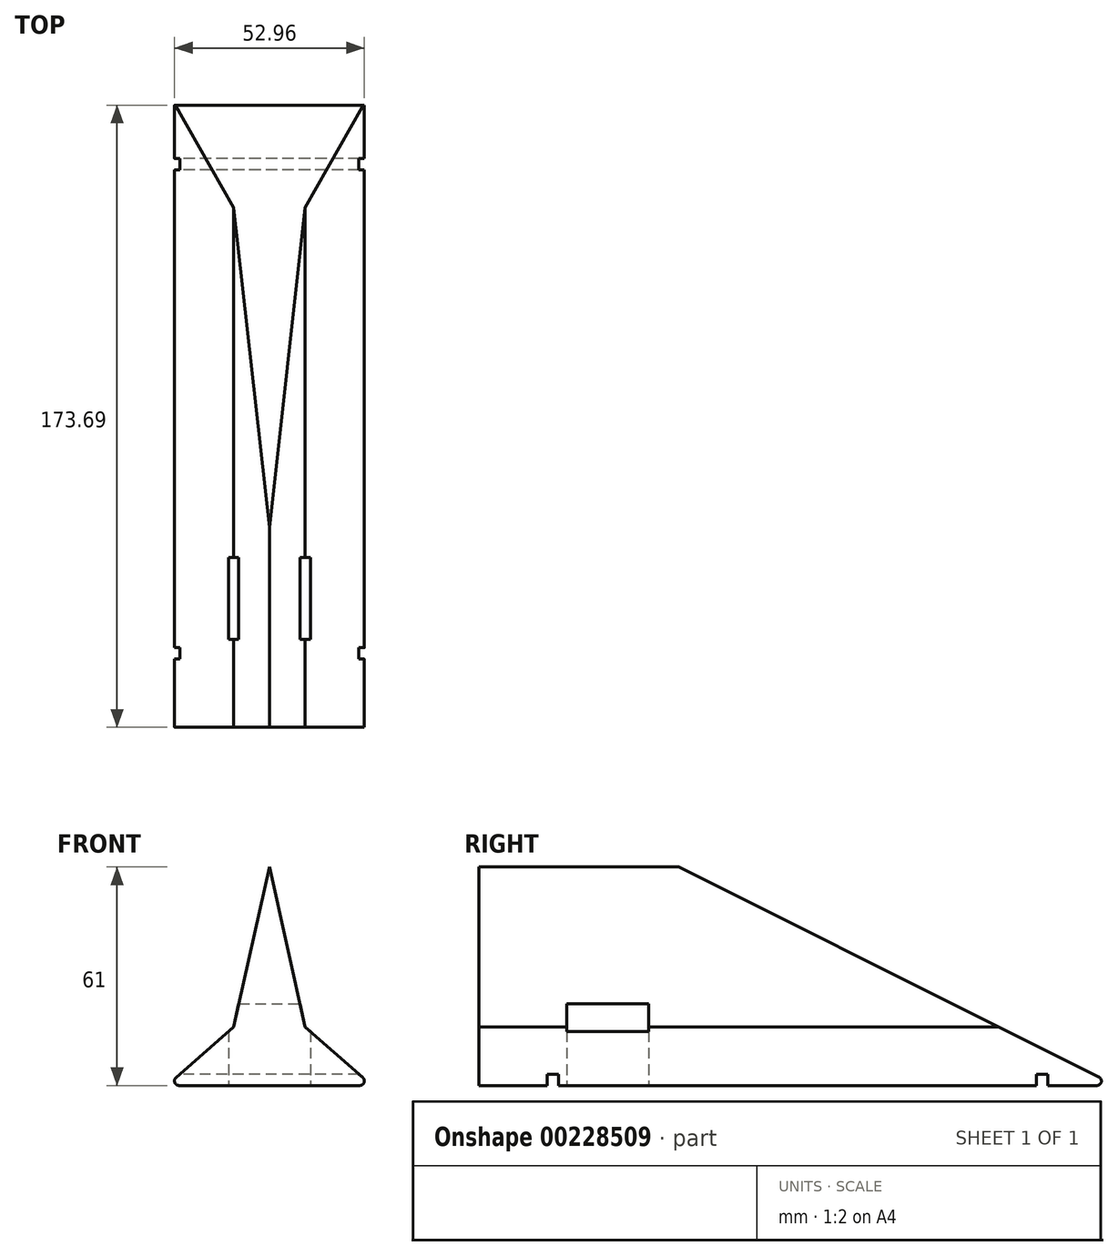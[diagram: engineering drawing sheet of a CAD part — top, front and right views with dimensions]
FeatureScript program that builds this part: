
annotation { "Feature Type Name" : "Feature", "Feature Type Description" : "" }
export const myFeature = defineFeature(function(context is Context, id is Id, definition is map)
    precondition{}
    {
        {
            var Q0;
            Q0=qCreatedBy(makeId("Right.planeOp"),FACE);
            var sketch = newSketch(context, id + "F0", { "sketchPlane" : qUnion([Q0])});
            skLineSegment(sketch, "E0", {"start": v(-57.94, 0) * mm, "end": v(-57.94, 88.9) * mm});
            skLineSegment(sketch, "E1", {"start": v(-57.94, 88.9) * mm, "end": v(119.86, 0) * mm});
            skLineSegment(sketch, "E2", {"start": v(-57.94, 0) * mm, "end": v(-38.9, 0) * mm});
            skLineSegment(sketch, "E3", {"start": v(-38.9, 0) * mm, "end": v(-38.9, 3.18) * mm});
            skLineSegment(sketch, "E4", {"start": v(-38.9, 3.18) * mm, "end": v(-35.72, 3.18) * mm});
            skLineSegment(sketch, "E5", {"start": v(-35.72, 3.18) * mm, "end": v(-35.72, 0) * mm});
            skLineSegment(sketch, "E6", {"start": v(119.86, 0) * mm, "end": v(100.8, 0) * mm});
            skLineSegment(sketch, "E7", {"start": v(100.8, 0) * mm, "end": v(100.8, 3.17) * mm});
            skLineSegment(sketch, "E8", {"start": v(100.8, 3.17) * mm, "end": v(97.63, 3.17) * mm});
            skLineSegment(sketch, "E9", {"start": v(97.63, 3.17) * mm, "end": v(97.63, 0) * mm});
            skLineSegment(sketch, "E10", {"start": v(97.63, 0) * mm, "end": v(-35.72, 0) * mm});
            skSolve(sketch);
        }
        {
            var Q0;
            Q0=makeQuery(id+"F0.imprint","IMPRINT",FACE,{"disambiguationData":[TD([[makeQuery(id+"F0.imprint","IMPRINT",EDGE,{"derivedFrom":sQuery(id+"F0.wireOp",EDGE,"E0")}),-1.0]])]});
            extrude(context, id + "F1", {"entities" : qUnion([Q0]), "endBound" : BoundingType.SYMMETRIC, "depth" : 57.15 * mm});
        }
        {
            var Q0;
            Q0=makeQuery(id+"F1.opExtrude","SWEPT_FACE",FACE,{"disambiguationData":[OSD([sQuery(id+"F0.wireOp",EDGE,"E10")])]});
            var sketch = newSketch(context, id + "F2", { "sketchPlane" : qUnion([Q0])});
            skLineSegment(sketch, "E11", {"start": v(0, 35.72) * mm, "end": v(0, -97.63) * mm, "construction": true});
            skLineSegment(sketch, "E12", {"start": v(0, 33.45) * mm, "end": v(11.43, 33.45) * mm});
            skLineSegment(sketch, "E13", {"start": v(11.43, 33.45) * mm, "end": v(11.43, 10.59) * mm});
            skLineSegment(sketch, "E14", {"start": v(11.43, 10.59) * mm, "end": v(0, 10.59) * mm});
            skLineSegment(sketch, "E15", {"start": v(0, 33.45) * mm, "end": v(-11.43, 33.45) * mm});
            skLineSegment(sketch, "E16", {"start": v(-11.43, 33.45) * mm, "end": v(-11.43, 10.59) * mm});
            skLineSegment(sketch, "E17", {"start": v(-11.43, 10.59) * mm, "end": v(0, 10.59) * mm});
            skSolve(sketch);
        }
        {
            var Q0;
            Q0=makeQuery(id+"F2.imprint","IMPRINT",FACE,{"disambiguationData":[TD([[makeQuery(id+"F2.imprint","IMPRINT",EDGE,{"derivedFrom":sQuery(id+"F2.wireOp",EDGE,"E12")}),-1.0]])]});
            extrude(context, id + "F3", {"entities" : qUnion([Q0]), "operationType" : NewBodyOperationType.REMOVE, "oppositeDirection" : true, "depth" : 22.86 * mm});
        }
        {
            var Q0;
            Q0=makeQuery(id+"F1.opExtrude","SWEPT_FACE",FACE,{"disambiguationData":[OSD([sQuery(id+"F0.wireOp",EDGE,"E0")])]});
            var sketch = newSketch(context, id + "F4", { "sketchPlane" : qUnion([Q0])});
            skLineSegment(sketch, "E18", {"start": v(-28.58, 0) * mm, "end": v(28.58, 0) * mm});
            skLineSegment(sketch, "E19", {"start": v(0, 61) * mm, "end": v(10, 16.38) * mm});
            skLineSegment(sketch, "E20", {"start": v(-10, 16.38) * mm, "end": v(0, 61) * mm});
            skLineSegment(sketch, "E21", {"start": v(-10, 16.38) * mm, "end": v(-28.58, 0) * mm});
            skLineSegment(sketch, "E22", {"start": v(10, 16.38) * mm, "end": v(28.58, 0) * mm});
            skSolve(sketch);
        }
        {
            var Q0;
            Q0=makeQuery(id+"F4.imprint","IMPRINT",FACE,{"disambiguationData":[TD([[makeQuery(id+"F4.imprint","IMPRINT",EDGE,{"derivedFrom":sQuery(id+"F4.wireOp",EDGE,"E18")}),-1.0]])]});
            extrude(context, id + "F5", {"entities" : qUnion([Q0]), "operationType" : NewBodyOperationType.INTERSECT, "oppositeDirection" : true, "depth" : 177.8 * mm});
        }
        {
            var Q0;
            Q0=makeQuery(id+"F1.opExtrude","SWEPT_EDGE",EDGE,{"disambiguationData":[OSD([sQuery(id+"F0.wireOp",EDGE,"E1"),sQuery(id+"F0.wireOp",EDGE,"E6")])]});
            var Q1;
            Q1=makeQuery(id+"F5.boolean.opBoolean","INTERSECT",EDGE,{"derivedFrom":[makeQuery(id+"F1.opExtrude","SWEPT_FACE",FACE,{"disambiguationData":[OSD([sQuery(id+"F0.wireOp",EDGE,"E1")])]}),makeQuery(id+"F5.boolean.toolComplement.opBoolean","COPY",FACE,{"derivedFrom":makeQuery(id+"F5.opExtrude","SWEPT_FACE",FACE,{"disambiguationData":[OSD([sQuery(id+"F4.wireOp",EDGE,"E19")])]})})]});
            var Q2;
            Q2=makeQuery(id+"F5.boolean.opBoolean","INTERSECT",EDGE,{"derivedFrom":[makeQuery(id+"F1.opExtrude","SWEPT_FACE",FACE,{"disambiguationData":[OSD([sQuery(id+"F0.wireOp",EDGE,"E1")])]}),makeQuery(id+"F5.boolean.toolComplement.opBoolean","COPY",FACE,{"derivedFrom":makeQuery(id+"F5.opExtrude","SWEPT_FACE",FACE,{"disambiguationData":[OSD([sQuery(id+"F4.wireOp",EDGE,"E20")])]})})]});
            var Q3;
            Q3=makeQuery(id+"F5.boolean.opBoolean","INTERSECT",EDGE,{"derivedFrom":[makeQuery(id+"F1.opExtrude","SWEPT_FACE",FACE,{"disambiguationData":[OSD([sQuery(id+"F0.wireOp",EDGE,"E1")])]}),makeQuery(id+"F5.boolean.toolComplement.opBoolean","COPY",FACE,{"derivedFrom":makeQuery(id+"F5.opExtrude","SWEPT_FACE",FACE,{"disambiguationData":[OSD([sQuery(id+"F4.wireOp",EDGE,"E22")])]})})]});
            var Q4;
            Q4=makeQuery(id+"F5.boolean.opBoolean","INTERSECT",EDGE,{"derivedFrom":[makeQuery(id+"F1.opExtrude","SWEPT_FACE",FACE,{"disambiguationData":[OSD([sQuery(id+"F0.wireOp",EDGE,"E1")])]}),makeQuery(id+"F5.boolean.toolComplement.opBoolean","COPY",FACE,{"derivedFrom":makeQuery(id+"F5.opExtrude","SWEPT_FACE",FACE,{"disambiguationData":[OSD([sQuery(id+"F4.wireOp",EDGE,"E21")])]})})]});
            var Q5;
            Q5=makeQuery(id+"F5.boolean.opBoolean","COPY",EDGE,{"derivedFrom":makeQuery(id+"F5.boolean.toolComplement.opBoolean","COPY",EDGE,{"derivedFrom":makeQuery(id+"F5.opExtrude","SWEPT_EDGE",EDGE,{"disambiguationData":[OSD([sQuery(id+"F4.wireOp",EDGE,"E19"),sQuery(id+"F4.wireOp",EDGE,"E20")])]})})});
            var Q6;
            {var subQ0=sQuery(id+"F4.wireOp",EDGE,"E19");var subQ1=sQuery(id+"F4.wireOp",EDGE,"E22");Q6=makeQuery(id+"F5.boolean.opBoolean","COPY",EDGE,{"disambiguationData":[TD([makeQuery(id+"F1.opExtrude","SWEPT_FACE",FACE,{"disambiguationData":[OSD([sQuery(id+"F0.wireOp",EDGE,"E1")])]})])],"derivedFrom":makeQuery(id+"F5.boolean.toolComplement.opBoolean","COPY",EDGE,{"derivedFrom":makeQuery(id+"F5.opExtrude","SWEPT_EDGE",EDGE,{"disambiguationData":[OSD([subQ0,subQ1])]})})});}
            var Q7;
            {var subQ0=sQuery(id+"F4.wireOp",EDGE,"E19");var subQ1=sQuery(id+"F4.wireOp",EDGE,"E22");Q7=makeQuery(id+"F5.boolean.opBoolean","COPY",EDGE,{"disambiguationData":[TD([makeQuery(id+"F1.opExtrude","SWEPT_FACE",FACE,{"disambiguationData":[OSD([sQuery(id+"F0.wireOp",EDGE,"E0")])]})])],"derivedFrom":makeQuery(id+"F5.boolean.toolComplement.opBoolean","COPY",EDGE,{"derivedFrom":makeQuery(id+"F5.opExtrude","SWEPT_EDGE",EDGE,{"disambiguationData":[OSD([subQ0,subQ1])]})})});}
            var Q8;
            Q8=makeQuery(id+"F5.boolean.opBoolean","MERGE",EDGE,{"derivedFrom":[makeQuery(id+"F1.opExtrude","CAP_EDGE",EDGE,{"disambiguationData":[OSD([sQuery(id+"F0.wireOp",EDGE,"E10")])],"isStart":false}),makeQuery(id+"F5.boolean.toolComplement.opBoolean","COPY",EDGE,{"derivedFrom":makeQuery(id+"F5.opExtrude","SWEPT_EDGE",EDGE,{"disambiguationData":[OSD([sQuery(id+"F0.wireOp",EDGE,"E0"),sQuery(id+"F4.wireOp",EDGE,"E18"),sQuery(id+"F4.wireOp",EDGE,"E22")])]})})]});
            var Q9;
            Q9=makeQuery(id+"F5.boolean.opBoolean","MERGE",EDGE,{"derivedFrom":[makeQuery(id+"F1.opExtrude","CAP_EDGE",EDGE,{"disambiguationData":[OSD([sQuery(id+"F0.wireOp",EDGE,"E2")])],"isStart":false}),makeQuery(id+"F5.boolean.toolComplement.opBoolean","COPY",EDGE,{"derivedFrom":makeQuery(id+"F5.opExtrude","SWEPT_EDGE",EDGE,{"disambiguationData":[OSD([sQuery(id+"F0.wireOp",EDGE,"E0"),sQuery(id+"F4.wireOp",EDGE,"E18"),sQuery(id+"F4.wireOp",EDGE,"E22")])]})})]});
            var Q10;
            Q10=makeQuery(id+"F5.boolean.opBoolean","MERGE",EDGE,{"derivedFrom":[makeQuery(id+"F1.opExtrude","CAP_EDGE",EDGE,{"disambiguationData":[OSD([sQuery(id+"F0.wireOp",EDGE,"E6")])],"isStart":false}),makeQuery(id+"F5.boolean.toolComplement.opBoolean","COPY",EDGE,{"derivedFrom":makeQuery(id+"F5.opExtrude","SWEPT_EDGE",EDGE,{"disambiguationData":[OSD([sQuery(id+"F0.wireOp",EDGE,"E0"),sQuery(id+"F4.wireOp",EDGE,"E18"),sQuery(id+"F4.wireOp",EDGE,"E22")])]})})]});
            var Q11;
            Q11=makeQuery(id+"F5.boolean.opBoolean","MERGE",EDGE,{"derivedFrom":[makeQuery(id+"F1.opExtrude","CAP_EDGE",EDGE,{"disambiguationData":[OSD([sQuery(id+"F0.wireOp",EDGE,"E6")])],"isStart":true}),makeQuery(id+"F5.boolean.toolComplement.opBoolean","COPY",EDGE,{"derivedFrom":makeQuery(id+"F5.opExtrude","SWEPT_EDGE",EDGE,{"disambiguationData":[OSD([sQuery(id+"F0.wireOp",EDGE,"E0"),sQuery(id+"F4.wireOp",EDGE,"E18"),sQuery(id+"F4.wireOp",EDGE,"E21")])]})})]});
            var Q12;
            Q12=makeQuery(id+"F5.boolean.opBoolean","MERGE",EDGE,{"derivedFrom":[makeQuery(id+"F1.opExtrude","CAP_EDGE",EDGE,{"disambiguationData":[OSD([sQuery(id+"F0.wireOp",EDGE,"E10")])],"isStart":true}),makeQuery(id+"F5.boolean.toolComplement.opBoolean","COPY",EDGE,{"derivedFrom":makeQuery(id+"F5.opExtrude","SWEPT_EDGE",EDGE,{"disambiguationData":[OSD([sQuery(id+"F0.wireOp",EDGE,"E0"),sQuery(id+"F4.wireOp",EDGE,"E18"),sQuery(id+"F4.wireOp",EDGE,"E21")])]})})]});
            var Q13;
            Q13=makeQuery(id+"F5.boolean.opBoolean","MERGE",EDGE,{"derivedFrom":[makeQuery(id+"F1.opExtrude","CAP_EDGE",EDGE,{"disambiguationData":[OSD([sQuery(id+"F0.wireOp",EDGE,"E2")])],"isStart":true}),makeQuery(id+"F5.boolean.toolComplement.opBoolean","COPY",EDGE,{"derivedFrom":makeQuery(id+"F5.opExtrude","SWEPT_EDGE",EDGE,{"disambiguationData":[OSD([sQuery(id+"F0.wireOp",EDGE,"E0"),sQuery(id+"F4.wireOp",EDGE,"E18"),sQuery(id+"F4.wireOp",EDGE,"E21")])]})})]});
            var Q14;
            {var subQ0=sQuery(id+"F4.wireOp",EDGE,"E20");var subQ1=sQuery(id+"F4.wireOp",EDGE,"E21");Q14=makeQuery(id+"F5.boolean.opBoolean","COPY",EDGE,{"disambiguationData":[TD([makeQuery(id+"F1.opExtrude","SWEPT_FACE",FACE,{"disambiguationData":[OSD([sQuery(id+"F0.wireOp",EDGE,"E0")])]})])],"derivedFrom":makeQuery(id+"F5.boolean.toolComplement.opBoolean","COPY",EDGE,{"derivedFrom":makeQuery(id+"F5.opExtrude","SWEPT_EDGE",EDGE,{"disambiguationData":[OSD([subQ0,subQ1])]})})});}
            var Q15;
            {var subQ0=sQuery(id+"F4.wireOp",EDGE,"E20");var subQ1=sQuery(id+"F4.wireOp",EDGE,"E21");Q15=makeQuery(id+"F5.boolean.opBoolean","COPY",EDGE,{"disambiguationData":[TD([makeQuery(id+"F1.opExtrude","SWEPT_FACE",FACE,{"disambiguationData":[OSD([sQuery(id+"F0.wireOp",EDGE,"E1")])]})])],"derivedFrom":makeQuery(id+"F5.boolean.toolComplement.opBoolean","COPY",EDGE,{"derivedFrom":makeQuery(id+"F5.opExtrude","SWEPT_EDGE",EDGE,{"disambiguationData":[OSD([subQ0,subQ1])]})})});}
            fillet(context, id + "F6", {"entities" : qUnion([Q0, Q1, Q2, Q3, Q4, Q5, Q6, Q7, Q8, Q9, Q10, Q11, Q12, Q13, Q14, Q15]), "radius" : 1.27 * mm, "tangentPropagation" : true, "allowEdgeOverflow" : false});
        }
    });
